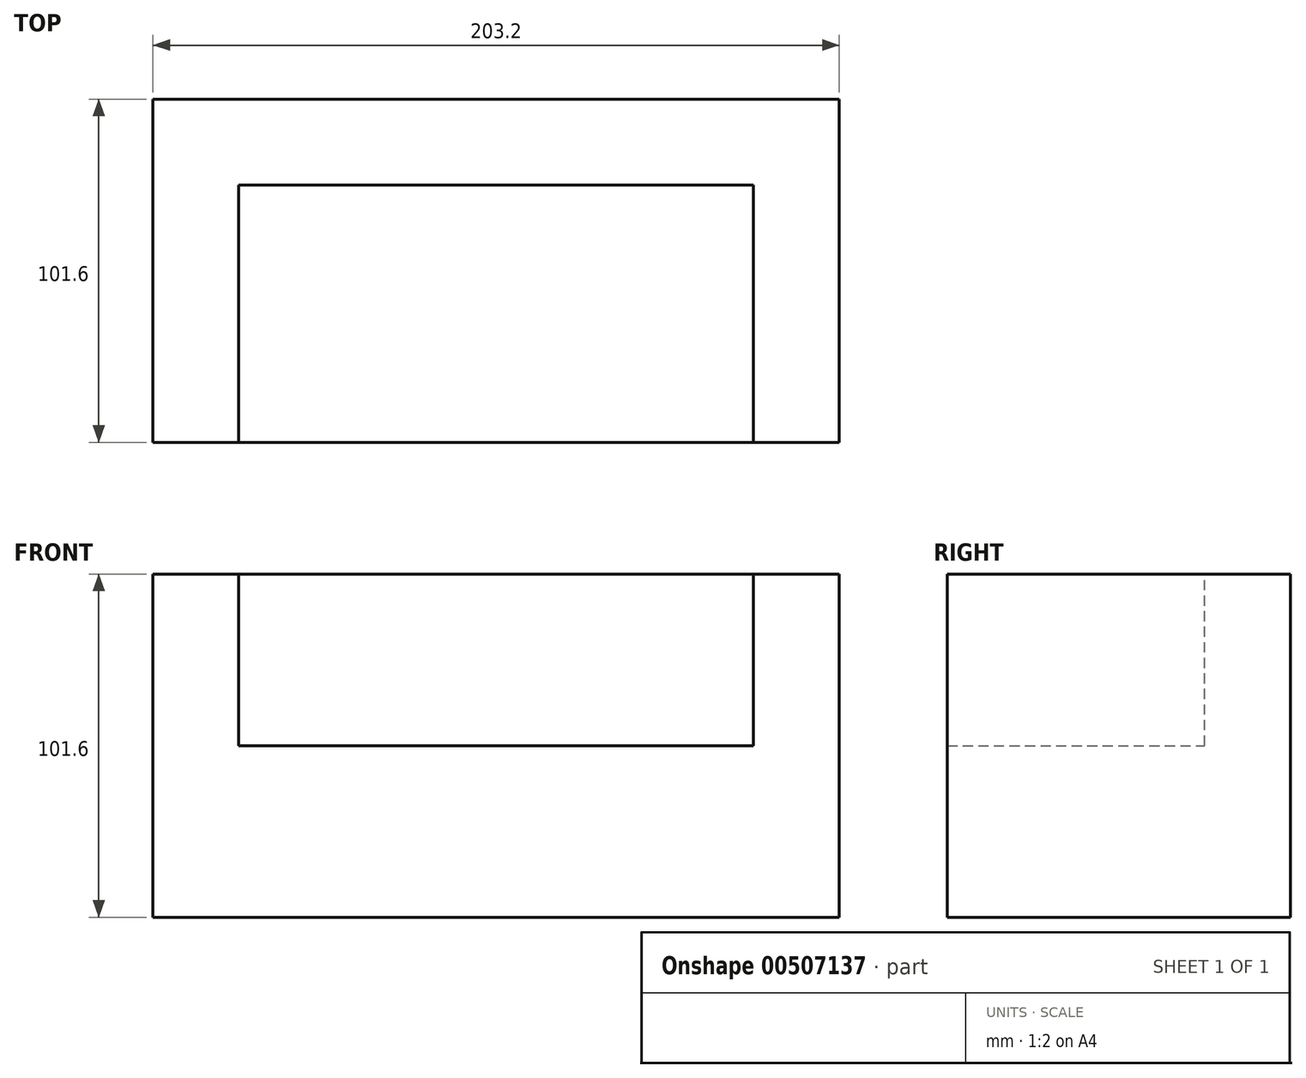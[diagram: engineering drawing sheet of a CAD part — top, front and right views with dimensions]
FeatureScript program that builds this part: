
annotation { "Feature Type Name" : "Feature", "Feature Type Description" : "" }
export const myFeature = defineFeature(function(context is Context, id is Id, definition is map)
    precondition{}
    {
        {
            var Q0;
            Q0=qCreatedBy(makeId("Front.planeOp"),FACE);
            var sketch = newSketch(context, id + "F0", { "sketchPlane" : qUnion([Q0])});
            skLineSegment(sketch, "E0.bottom", {"start": v(101.6, -50.8) * mm, "end": v(-101.6, -50.8) * mm});
            skLineSegment(sketch, "E0.top", {"start": v(101.6, 50.8) * mm, "end": v(-101.6, 50.8) * mm});
            skLineSegment(sketch, "E0.left", {"start": v(101.6, -50.8) * mm, "end": v(101.6, 50.8) * mm});
            skLineSegment(sketch, "E0.right", {"start": v(-101.6, -50.8) * mm, "end": v(-101.6, 50.8) * mm});
            skPoint(sketch, "E0.middle", {"position": v(0, 0) * mm});
            skSolve(sketch);
        }
        {
            var Q0;
            Q0 = qSketchRegion(id + "F0", true);
            extrude(context, id + "F1", {"entities" : qUnion([Q0]), "depth" : 101.6 * mm});
        }
        {
            var Q0;
            Q0=makeQuery(id+"F1.opExtrude","SWEPT_FACE",FACE,{"disambiguationData":[OSD([sQuery(id+"F0.wireOp",EDGE,"E0.top")])]});
            var sketch = newSketch(context, id + "F2", { "sketchPlane" : qUnion([Q0])});
            skLineSegment(sketch, "E1.bottom", {"start": v(-76.2, -101.6) * mm, "end": v(76.2, -101.6) * mm});
            skLineSegment(sketch, "E1.top", {"start": v(-76.2, -25.4) * mm, "end": v(76.2, -25.4) * mm});
            skLineSegment(sketch, "E1.left", {"start": v(-76.2, -101.6) * mm, "end": v(-76.2, -25.4) * mm});
            skLineSegment(sketch, "E1.right", {"start": v(76.2, -101.6) * mm, "end": v(76.2, -25.4) * mm});
            skSolve(sketch);
        }
        {
            var Q0;
            Q0 = qSketchRegion(id + "F2", true);
            extrude(context, id + "F3", {"entities" : qUnion([Q0]), "operationType" : NewBodyOperationType.REMOVE, "oppositeDirection" : true, "depth" : 50.8 * mm});
        }
    });
